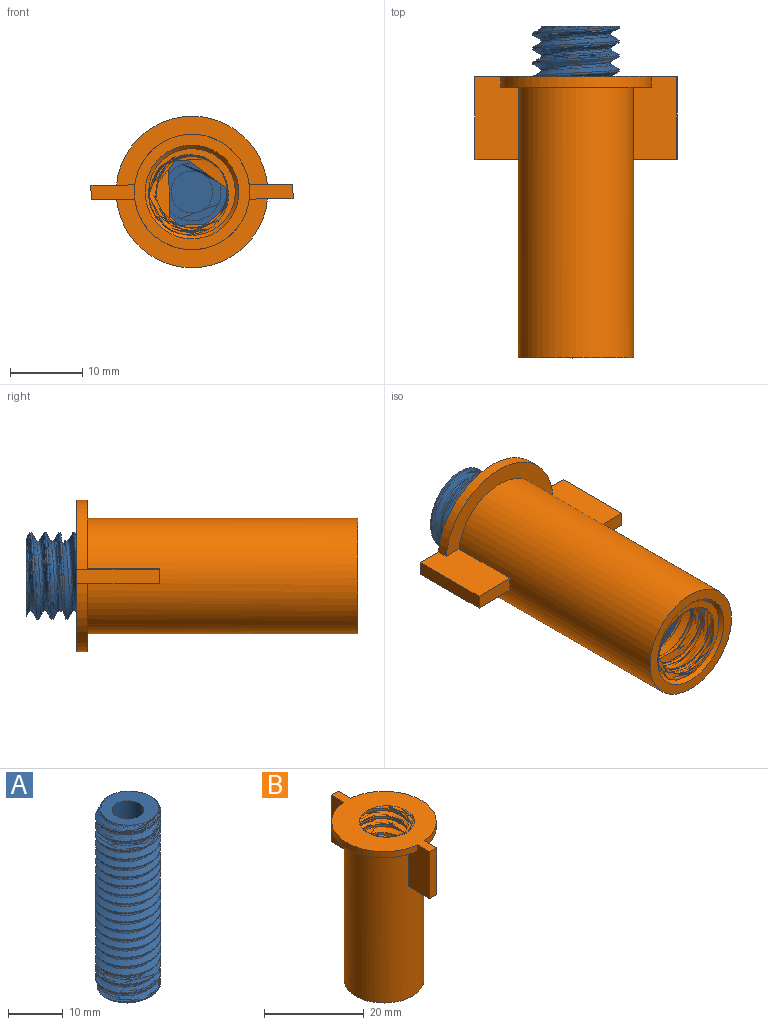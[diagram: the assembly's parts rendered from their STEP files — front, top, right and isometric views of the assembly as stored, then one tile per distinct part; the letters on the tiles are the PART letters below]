
ASSEMBLY  parts=2 mates=1
PART A: 12 faces, bbox 12.6x14.4x41.2 mm
  f0: cylinder r=6mm len=39mm, axis (0,0,-1), area 281.5mm2, adj f2,f5,f10,f11
  f1: cylinder r=2.9mm len=20mm, axis (0,0,-1), area 364.4mm2, adj f2,f3
  f2: plane 11.39x11.32mm, normal (0,0,1), area 64.8mm2, adj f0,f1,f9,f10,f11
  f3: plane 5.8x5.8mm, normal (0,0,1), area 26.4mm2, adj f1
  f4: cylinder r=4.03mm len=15mm, axis (0,0,1), area 379.3mm2, adj f5,f8
  f5: plane 11.39x11.32mm, normal (0,0,-1), area 40.4mm2, adj f0,f4,f9,f10,f11
  f6: plane 5.8x5.8mm, normal (0,0,-1), area 26.4mm2, adj f7
  f7: cylinder r=2.9mm len=15mm, axis (0,0,1), area 273.3mm2, adj f6,f8
  f8: plane 8.05x8.05mm, normal (0,0,-1), area 24.5mm2, adj f4,f7
  f9: bspline ~40.5x11.36mm, area 332.3mm2, adj f2,f5,f10,f11
  f10: bspline ~40.63x13.86mm, area 837.7mm2, adj f0,f2,f5,f9
  f11: bspline ~40.29x13.86mm, area 838.3mm2, adj f0,f2,f5,f9
PART B: 22 faces, bbox 21.6x28.6x40.6 mm
  f0: cylinder r=10.5mm len=20.9mm, axis (0,0,1), area 46.5mm2, adj f1,f5,f7,f11
  f1: plane 20.9x9.5mm, normal (0,0,-1), area 67.6mm2, adj f0,f3,f7,f11
  f2: cylinder r=10.5mm len=20.9mm, axis (0,0,1), area 46.5mm2, adj f5,f6,f9,f12
  f3: cylinder r=8mm len=37.5mm, axis (0,0,1), area 1844.9mm2, adj f1,f4,f6,f7,f9,f10,f11,f12
  f4: plane 16x16mm, normal (0,0,-1), area 68.3mm2, adj f3,f15
  f5: plane 28.56x21.56mm, normal (0,0,1), area 265.6mm2, adj f0,f2,f7,f8,f9,f11,f12,f13
  f6: plane 20.9x9.5mm, normal (0,0,-1), area 67.6mm2, adj f2,f3,f9,f12
  f7: plane 11.5x6.06mm, normal (-1,0,0), area 65.9mm2, adj f0,f1,f3,f5,f8,f10
  f8: plane 11.5x2mm, normal (0,1,0), area 23mm2, adj f5,f7,f9,f10
  f9: plane 11.5x6.06mm, normal (1,0,0), area 65.9mm2, adj f2,f3,f5,f6,f8,f10
  f10: plane 6.06x2mm, normal (0,0,-1), area 12mm2, adj f3,f7,f8,f9
  f11: plane 11.5x6.06mm, normal (-1,0,0), area 65.9mm2, adj f0,f1,f3,f5,f13,f14
  f12: plane 11.5x6.06mm, normal (1,0,0), area 65.9mm2, adj f2,f3,f5,f6,f13,f14
  f13: plane 11.5x2mm, normal (0,-1,0), area 23mm2, adj f5,f11,f12,f14
  f14: plane 6.06x2mm, normal (0,0,-1), area 12mm2, adj f3,f11,f12,f13
  f15: cone r=6.5mm half-angle=45deg, axis (0,0,-1), area 27.8mm2, adj f4,f19,f20
  f16: bspline ~39.96x14.05mm, area 838.1mm2, adj f5,f18,f19,f20,f21
  f17: bspline ~39.96x14.05mm, area 835.8mm2, adj f5,f18,f19,f20,f21
  f18: bspline ~39.25x14.26mm, area 213.9mm2, adj f5,f16,f17,f19
  f19: plane 4.53x4.45mm, normal (0,0,1), area 0.7mm2, adj f15,f16,f17,f18
  f20: plane 12.49x12.49mm, normal (0,0,-1), area 18.9mm2, adj f15,f16,f17,f21
  f21: cylinder r=5mm len=38.5mm, axis (0,0,1), area 344.4mm2, adj f5,f16,f17,f20
PLACE A rot(axis=(-1,0,0),90deg) t=(0,-4.5,4.5)mm fixed
PLACE B rot(axis=(-0.58,-0.58,-0.58),120.1deg) t=(0,12.5,4.5)mm
MATE cylindrical A.f0 <-> B.f0  axis (0,-1,0) through (0,19.5,4.5)mm
